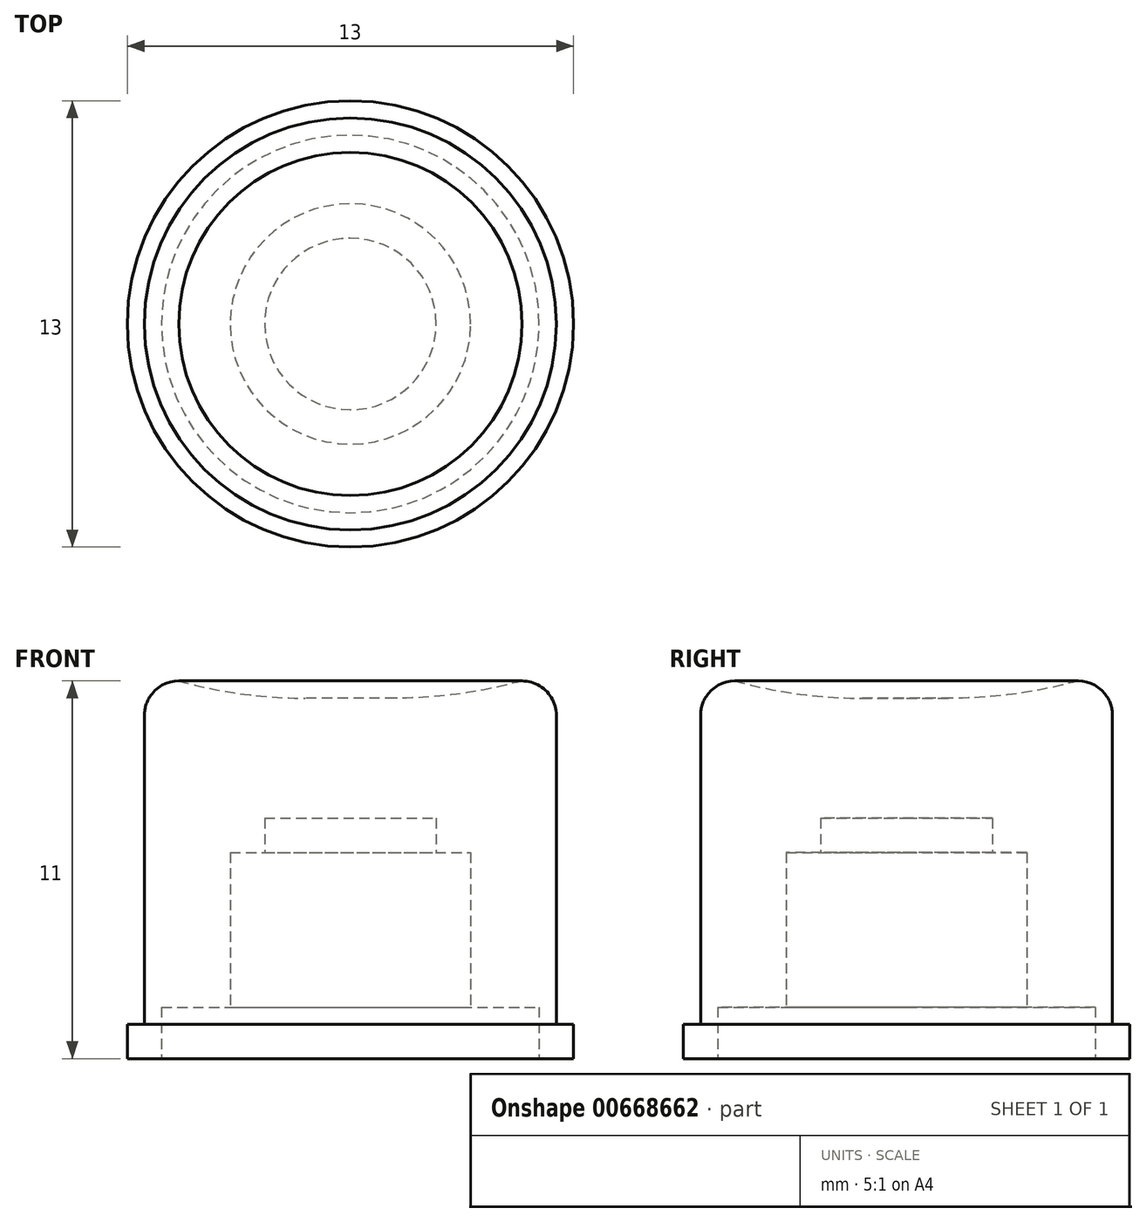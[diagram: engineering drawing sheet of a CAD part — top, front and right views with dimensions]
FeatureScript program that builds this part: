
annotation { "Feature Type Name" : "Feature", "Feature Type Description" : "" }
export const myFeature = defineFeature(function(context is Context, id is Id, definition is map)
    precondition{}
    {
        {
            var Q0;
            Q0=qCreatedBy(makeId("Top.planeOp"),FACE);
            var sketch = newSketch(context, id + "F0", { "sketchPlane" : qUnion([Q0])});
            skCircle(sketch, "E0", {"center": v(0, 0) * mm, "radius": 6.5 * mm});
            skSolve(sketch);
        }
        {
            var Q0;
            Q0=makeQuery(id+"F0.imprint","IMPRINT",FACE,{"disambiguationData":[TD([[makeQuery(id+"F0.imprint","IMPRINT",EDGE,{"derivedFrom":sQuery(id+"F0.wireOp",EDGE,"E0")}),1.0]])]});
            extrude(context, id + "F1", {"entities" : qUnion([Q0]), "flatOperationType" : FlatOperationType.REMOVE, "depth" : 1 * mm, "offsetDistance" : 25 * mm, "domain" : OperationDomain.MODEL});
        }
        {
            var Q0;
            Q0=makeQuery(id+"F1.opExtrude","CAP_FACE",FACE,{"disambiguationData":[OSD([sQuery(id+"F0.wireOp",EDGE,"E0")])],"isStart":false});
            var sketch = newSketch(context, id + "F2", { "sketchPlane" : qUnion([Q0])});
            skCircle(sketch, "E1", {"center": v(0, 0) * mm, "radius": 6 * mm});
            skSolve(sketch);
        }
        {
            var Q0;
            Q0=makeQuery(id+"F2.imprint","IMPRINT",FACE,{"disambiguationData":[TD([[makeQuery(id+"F2.imprint","IMPRINT",EDGE,{"derivedFrom":sQuery(id+"F2.wireOp",EDGE,"E1")}),1.0]])]});
            extrude(context, id + "F3", {"entities" : qUnion([Q0]), "operationType" : NewBodyOperationType.ADD, "flatOperationType" : FlatOperationType.REMOVE, "depth" : 10 * mm, "offsetDistance" : 25 * mm, "domain" : OperationDomain.MODEL});
        }
        {
            var Q0;
            Q0=makeQuery(id+"F3.opExtrude","CAP_EDGE",EDGE,{"disambiguationData":[OSD([sQuery(id+"F2.wireOp",EDGE,"E1")])],"isStart":false});
            fillet(context, id + "F4", {"entities" : qUnion([Q0]), "radius" : 1 * mm, "tangentPropagation" : true, "defaultsChanged" : false, "vertexSettings" : [], "allowEdgeOverflow" : false});
        }
        {
            var Q0;
            Q0=makeQuery(id+"F1.opExtrude","CAP_FACE",FACE,{"disambiguationData":[OSD([sQuery(id+"F0.wireOp",EDGE,"E0")])],"isStart":true});
            var sketch = newSketch(context, id + "F5", { "sketchPlane" : qUnion([Q0])});
            skCircle(sketch, "E2", {"center": v(0, 0) * mm, "radius": 5.5 * mm});
            skCircle(sketch, "E3", {"center": v(0, 0) * mm, "radius": 3.5 * mm});
            skSolve(sketch);
        }
        {
            var Q0;
            Q0=makeQuery(id+"F5.imprint","IMPRINT",FACE,{"disambiguationData":[TD([[makeQuery(id+"F5.imprint","IMPRINT",EDGE,{"derivedFrom":sQuery(id+"F5.wireOp",EDGE,"E2")}),1.0]])]});
            extrude(context, id + "F6", {"entities" : qUnion([Q0]), "operationType" : NewBodyOperationType.REMOVE, "oppositeDirection" : true, "depth" : 1.5 * mm, "offsetDistance" : 25 * mm});
        }
        {
            var Q0;
            Q0=makeQuery(id+"F6.boolean.opBoolean","SPLIT",FACE,{"disambiguationData":[TD([makeQuery(id+"F6.opExtrude","SWEPT_FACE",FACE,{"disambiguationData":[OSD([sQuery(id+"F5.wireOp",EDGE,"E3")])]})])],"derivedFrom":makeQuery(id+"F1.opExtrude","CAP_FACE",FACE,{"disambiguationData":[OSD([sQuery(id+"F0.wireOp",EDGE,"E0")])],"isStart":true})});
            extrude(context, id + "F7", {"entities" : qUnion([Q0]), "operationType" : NewBodyOperationType.REMOVE, "oppositeDirection" : true, "depth" : 6 * mm, "offsetDistance" : 25 * mm});
        }
        {
            var Q0;
            Q0=makeQuery(id+"F7.boolean.opBoolean","COPY",FACE,{"derivedFrom":makeQuery(id+"F7.opExtrude","CAP_FACE",FACE,{"disambiguationData":[OSD([sQuery(id+"F0.wireOp",EDGE,"E0")])],"isStart":false})});
            var sketch = newSketch(context, id + "F8", { "sketchPlane" : qUnion([Q0])});
            skCircle(sketch, "E4", {"center": v(0, 0) * mm, "radius": 2.5 * mm});
            skSolve(sketch);
        }
        {
            var Q0;
            Q0=makeQuery(id+"F8.imprint","IMPRINT",FACE,{"disambiguationData":[TD([[makeQuery(id+"F8.imprint","IMPRINT",EDGE,{"derivedFrom":sQuery(id+"F8.wireOp",EDGE,"E4")}),1.0]])]});
            extrude(context, id + "F9", {"entities" : qUnion([Q0]), "operationType" : NewBodyOperationType.REMOVE, "oppositeDirection" : true, "depth" : 1 * mm, "offsetDistance" : 25 * mm});
        }
        {
            var Q0;
            Q0=makeQuery(id+"F3.opExtrude","CAP_FACE",FACE,{"disambiguationData":[OSD([sQuery(id+"F2.wireOp",EDGE,"E1")])],"isStart":false});
            extrude(context, id + "F10", {"entities" : qUnion([Q0]), "operationType" : NewBodyOperationType.REMOVE, "oppositeDirection" : true, "depth" : 0.5 * mm, "offsetDistance" : 25 * mm});
        }
        {
            var Q0;
            Q0=makeQuery(id+"F10.boolean.opBoolean","COPY",EDGE,{"derivedFrom":makeQuery(id+"F10.opExtrude","CAP_EDGE",EDGE,{"disambiguationData":[OSD([sQuery(id+"F2.wireOp",EDGE,"E1")])],"isStart":false})});
            fillet(context, id + "F11", {"entities" : qUnion([Q0]), "radius" : 13.86 * mm, "tangentPropagation" : true, "allowEdgeOverflow" : false});
        }
    });
